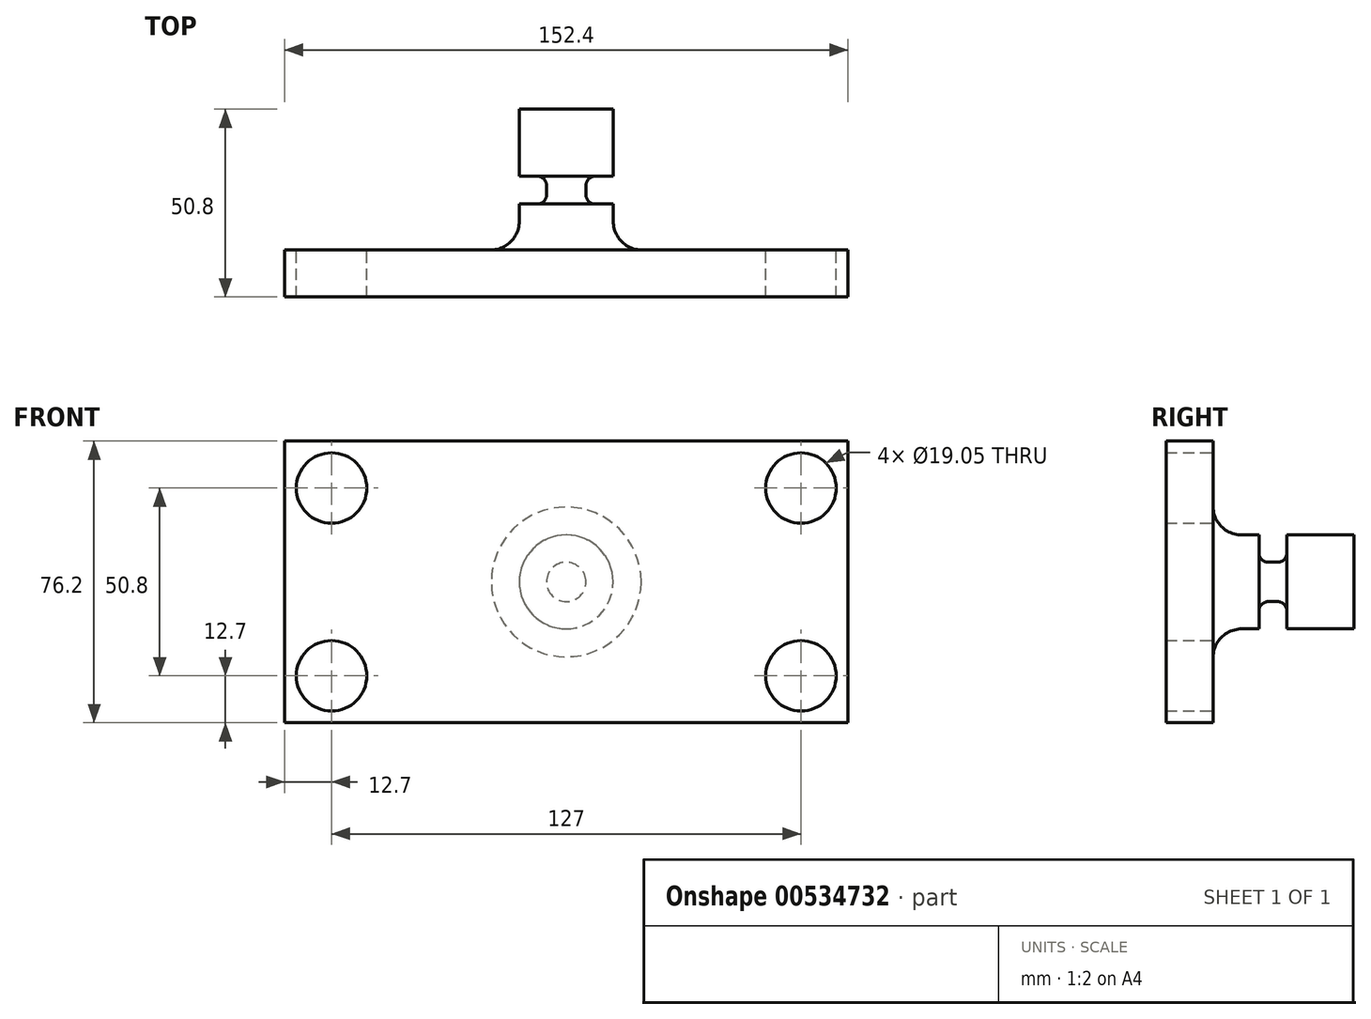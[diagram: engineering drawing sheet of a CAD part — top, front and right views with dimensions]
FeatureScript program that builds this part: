
annotation { "Feature Type Name" : "Feature", "Feature Type Description" : "" }
export const myFeature = defineFeature(function(context is Context, id is Id, definition is map)
    precondition{}
    {
        {
            var Q0;
            Q0=qCreatedBy(makeId("Front.planeOp"),FACE);
            var sketch = newSketch(context, id + "F0", { "sketchPlane" : qUnion([Q0])});
            skLineSegment(sketch, "E0.bottom", {"start": v(76.2, -38.1) * mm, "end": v(-76.2, -38.1) * mm});
            skLineSegment(sketch, "E0.top", {"start": v(76.2, 38.1) * mm, "end": v(-76.2, 38.1) * mm});
            skLineSegment(sketch, "E0.left", {"start": v(76.2, -38.1) * mm, "end": v(76.2, 38.1) * mm});
            skLineSegment(sketch, "E0.right", {"start": v(-76.2, -38.1) * mm, "end": v(-76.2, 38.1) * mm});
            skPoint(sketch, "E0.middle", {"position": v(0, 0) * mm});
            skSolve(sketch);
        }
        {
            var Q0;
            Q0=makeQuery(id+"F0.imprint","IMPRINT",FACE,{"disambiguationData":[TD([[makeQuery(id+"F0.imprint","IMPRINT",EDGE,{"derivedFrom":sQuery(id+"F0.wireOp",EDGE,"E0.bottom")}),-1.0]])]});
            extrude(context, id + "F1", {"entities" : qUnion([Q0]), "depth" : 12.7 * mm, "offsetDistance" : 25.4 * mm});
        }
        {
            var Q0;
            Q0=makeQuery(id+"F1.opExtrude","CAP_FACE",FACE,{"disambiguationData":[OSD([sQuery(id+"F0.wireOp",EDGE,"E0.bottom"),sQuery(id+"F0.wireOp",EDGE,"E0.top"),sQuery(id+"F0.wireOp",EDGE,"E0.left"),sQuery(id+"F0.wireOp",EDGE,"E0.right")])],"isStart":true});
            var sketch = newSketch(context, id + "F2", { "sketchPlane" : qUnion([Q0])});
            skLineSegment(sketch, "E1.top", {"start": v(-63.5, -25.4) * mm, "end": v(63.5, -25.4) * mm, "construction": true});
            skLineSegment(sketch, "E1.left", {"start": v(-63.5, 25.4) * mm, "end": v(-63.5, -25.4) * mm, "construction": true});
            skPoint(sketch, "E1.middle", {"position": v(0, 0) * mm});
            skCircle(sketch, "E2", {"center": v(63.5, 25.4) * mm, "radius": 9.53 * mm});
            skCircle(sketch, "E3", {"center": v(63.5, -25.4) * mm, "radius": 9.53 * mm});
            skCircle(sketch, "E4", {"center": v(-63.5, -25.4) * mm, "radius": 9.53 * mm});
            skCircle(sketch, "E5", {"center": v(-63.5, 25.4) * mm, "radius": 9.53 * mm});
            skSolve(sketch);
        }
        {
            var Q0;
            Q0=makeQuery(id+"F2.imprint","IMPRINT",FACE,{"disambiguationData":[TD([[makeQuery(id+"F2.imprint","IMPRINT",EDGE,{"derivedFrom":sQuery(id+"F2.wireOp",EDGE,"E2")}),1.0]])]});
            var Q1;
            Q1=makeQuery(id+"F2.imprint","IMPRINT",FACE,{"disambiguationData":[TD([[makeQuery(id+"F2.imprint","IMPRINT",EDGE,{"derivedFrom":sQuery(id+"F2.wireOp",EDGE,"E3")}),1.0]])]});
            var Q2;
            Q2=makeQuery(id+"F2.imprint","IMPRINT",FACE,{"disambiguationData":[TD([[makeQuery(id+"F2.imprint","IMPRINT",EDGE,{"derivedFrom":sQuery(id+"F2.wireOp",EDGE,"E4")}),1.0]])]});
            var Q3;
            Q3=makeQuery(id+"F2.imprint","IMPRINT",FACE,{"disambiguationData":[TD([[makeQuery(id+"F2.imprint","IMPRINT",EDGE,{"derivedFrom":sQuery(id+"F2.wireOp",EDGE,"E5")}),1.0]])]});
            extrude(context, id + "F3", {"entities" : qUnion([Q0, Q1, Q2, Q3]), "operationType" : NewBodyOperationType.REMOVE, "endBound" : BoundingType.THROUGH_ALL, "oppositeDirection" : true, "depth" : 25.4 * mm, "offsetDistance" : 25.4 * mm});
        }
        {
            var Q0;
            Q0=qCreatedBy(makeId("Top.planeOp"),FACE);
            var sketch = newSketch(context, id + "F4", { "sketchPlane" : qUnion([Q0])});
            skLineSegment(sketch, "E6.bottom", {"start": v(0, 0) * mm, "end": v(-12.7, 0) * mm});
            skLineSegment(sketch, "E6.top", {"start": v(0, 38.1) * mm, "end": v(-12.7, 38.1) * mm});
            skLineSegment(sketch, "E6.left", {"start": v(0, 0) * mm, "end": v(0, 38.1) * mm});
            skLineSegment(sketch, "E6.right", {"start": v(-12.7, 0) * mm, "end": v(-12.7, 38.1) * mm});
            skLineSegment(sketch, "E7", {"start": v(-12.7, 0) * mm, "end": v(-20.75, 0) * mm});
            skLineSegment(sketch, "E8", {"start": v(-20.75, 0) * mm, "end": v(-12.7, 0) * mm});
            skLineSegment(sketch, "E9", {"start": v(-12.7, 7.8) * mm, "end": v(-12.7, 0) * mm});
            skArc(sketch, "E10", {"start": v(-20.75, 0) * mm, "mid": v(-15.07, 2.2) * mm, "end": v(-12.7, 7.8) * mm});
            skSolve(sketch);
        }
        {
            var Q0;
            Q0 = qSketchRegion(id + "F4", true);
            var Q1;
            Q1=sQuery(id+"F4.wireOp",EDGE,"E6.left");
            revolve(context, id + "F5", {"operationType" : NewBodyOperationType.ADD, "entities" : qUnion([Q0]), "axis" : qUnion([Q1]), "revolveType" : RevolveType.FULL});
        }
        {
            var Q0;
            Q0=qCreatedBy(makeId("Top.planeOp"),FACE);
            var sketch = newSketch(context, id + "F6", { "sketchPlane" : qUnion([Q0])});
            skLineSegment(sketch, "E11", {"start": v(0, 0) * mm, "end": v(0, 16.2) * mm, "construction": true});
            skLineSegment(sketch, "E12", {"start": v(0, 16.2) * mm, "end": v(-10.65, 16.2) * mm, "construction": true});
            skLineSegment(sketch, "E13.bottom", {"start": v(-7.86, 12.42) * mm, "end": v(-15.97, 12.42) * mm});
            skLineSegment(sketch, "E13.top", {"start": v(-7.86, 19.98) * mm, "end": v(-15.97, 19.98) * mm});
            skLineSegment(sketch, "E13.left", {"start": v(-5.32, 14.96) * mm, "end": v(-5.32, 17.44) * mm});
            skLineSegment(sketch, "E13.right", {"start": v(-15.97, 12.42) * mm, "end": v(-15.97, 19.98) * mm});
            skPoint(sketch, "E13.middle", {"position": v(-10.65, 16.2) * mm});
            skPoint(sketch, "E13.cornerSnap0", {"position": v(-5.32, 16.2) * mm});
            skPoint(sketch, "E14.visualSharp", {"position": v(-5.32, 19.98) * mm});
            skArc(sketch, "E14.filletArc", {"start": v(-5.32, 17.44) * mm, "mid": v(-6.07, 19.23) * mm, "end": v(-7.86, 19.98) * mm});
            skPoint(sketch, "E15.visualSharp", {"position": v(-5.32, 12.42) * mm});
            skArc(sketch, "E15.filletArc", {"start": v(-7.86, 12.42) * mm, "mid": v(-6.07, 13.16) * mm, "end": v(-5.32, 14.96) * mm});
            skSolve(sketch);
        }
        {
            var Q0;
            Q0=makeQuery(id+"F6.imprint","IMPRINT",FACE,{"disambiguationData":[TD([[makeQuery(id+"F6.imprint","IMPRINT",EDGE,{"derivedFrom":sQuery(id+"F6.wireOp",EDGE,"E13.bottom")}),-1.0]])]});
            var Q1;
            Q1=sQuery(id+"F6.wireOp",EDGE,"E11");
            revolve(context, id + "F7", {"operationType" : NewBodyOperationType.REMOVE, "entities" : qUnion([Q0]), "axis" : qUnion([Q1]), "revolveType" : RevolveType.FULL, "oppositeDirection" : true});
        }
    });
